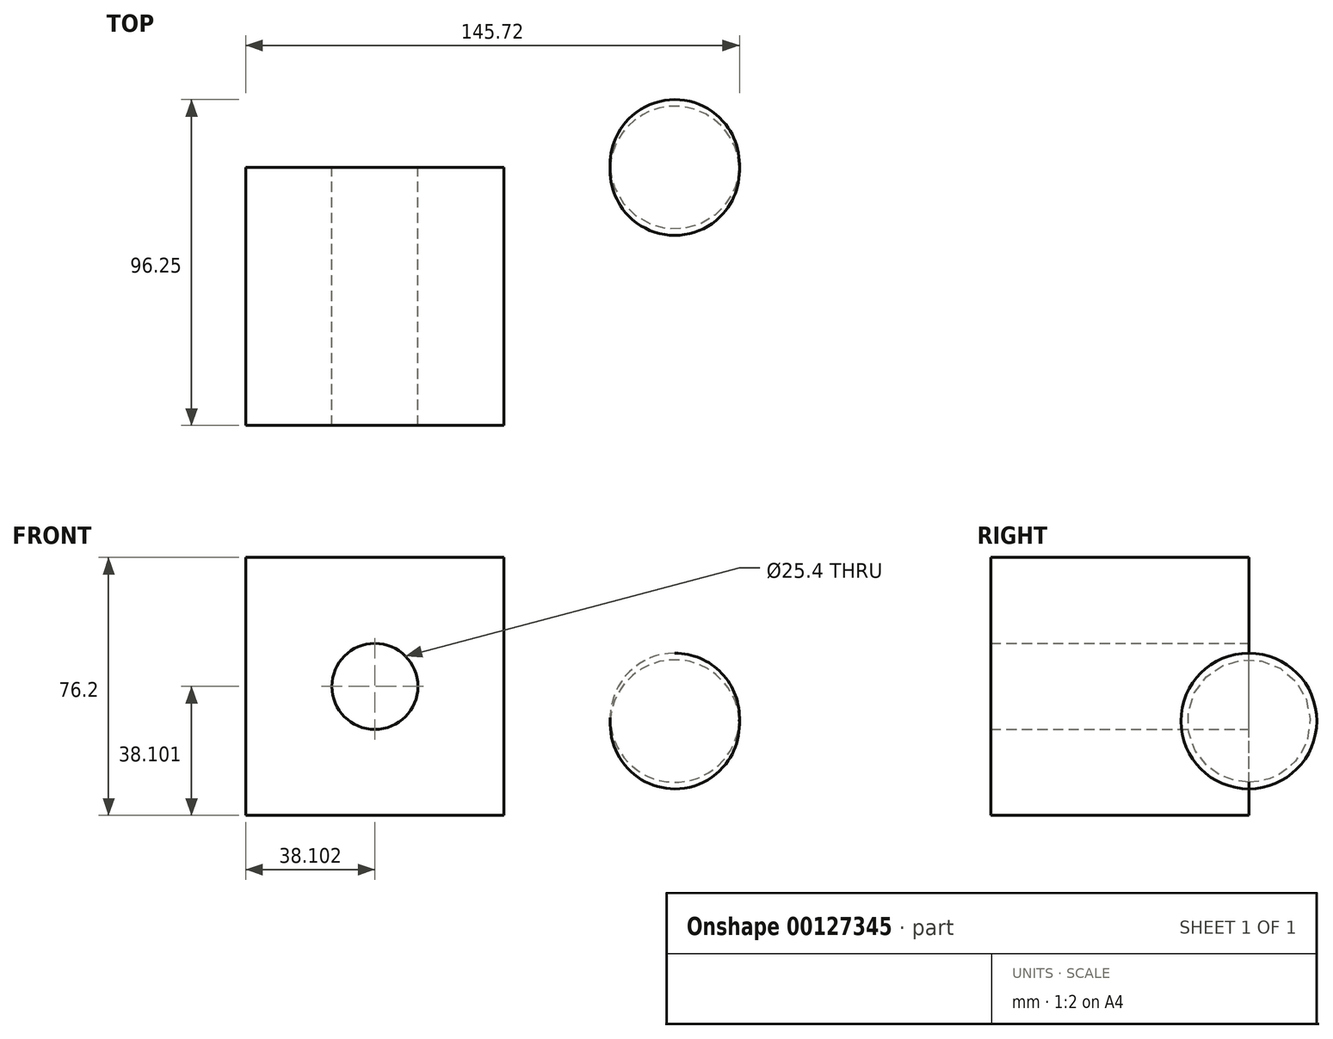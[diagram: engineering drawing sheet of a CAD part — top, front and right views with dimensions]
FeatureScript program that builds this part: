
annotation { "Feature Type Name" : "Feature", "Feature Type Description" : "" }
export const myFeature = defineFeature(function(context is Context, id is Id, definition is map)
    precondition{}
    {
        {
            var Q0;
            Q0=qCreatedBy(makeId("Front.planeOp"),FACE);
            var sketch = newSketch(context, id + "F0", { "sketchPlane" : qUnion([Q0])});
            skLineSegment(sketch, "E0.bottom", {"start": v(-63.5, -27.9) * mm, "end": v(12.7, -27.9) * mm});
            skLineSegment(sketch, "E0.top", {"start": v(-63.5, 48.3) * mm, "end": v(12.7, 48.3) * mm});
            skLineSegment(sketch, "E0.left", {"start": v(-63.5, -27.9) * mm, "end": v(-63.5, 48.3) * mm});
            skLineSegment(sketch, "E0.right", {"start": v(12.7, -27.9) * mm, "end": v(12.7, 48.3) * mm});
            skLineSegment(sketch, "E1", {"start": v(-63.5, 48.3) * mm, "end": v(12.7, -27.9) * mm});
            skLineSegment(sketch, "E2", {"start": v(12.7, 48.3) * mm, "end": v(-63.5, -27.9) * mm});
            skCircle(sketch, "E3", {"center": v(-25.4, 10.2) * mm, "radius": 12.7 * mm});
            skSolve(sketch);
        }
        {
            var Q0;
            Q0 = qSketchRegion(id + "F0", true);
            extrude(context, id + "F1", {"entities" : qUnion([Q0]), "depth" : 76.2 * mm});
        }
        {
            var Q0;
            Q0=qCreatedBy(makeId("Front.planeOp"),FACE);
            var sketch = newSketch(context, id + "F2", { "sketchPlane" : qUnion([Q0])});
            skLineSegment(sketch, "E4", {"start": v(44.1, 0) * mm, "end": v(82.2, 0) * mm});
            skArc(sketch, "E5", {"start": v(82.2, 0) * mm, "mid": v(63.15, 18.1) * mm, "end": v(44.1, 0) * mm});
            skSolve(sketch);
        }
        {
            var Q0;
            Q0 = qSketchRegion(id + "F2", true);
            var Q1;
            Q1=sQuery(id+"F2.wireOp",EDGE,"E4");
            revolve(context, id + "F3", {"entities" : qUnion([Q0]), "axis" : qUnion([Q1]), "revolveType" : RevolveType.FULL});
        }
    });
